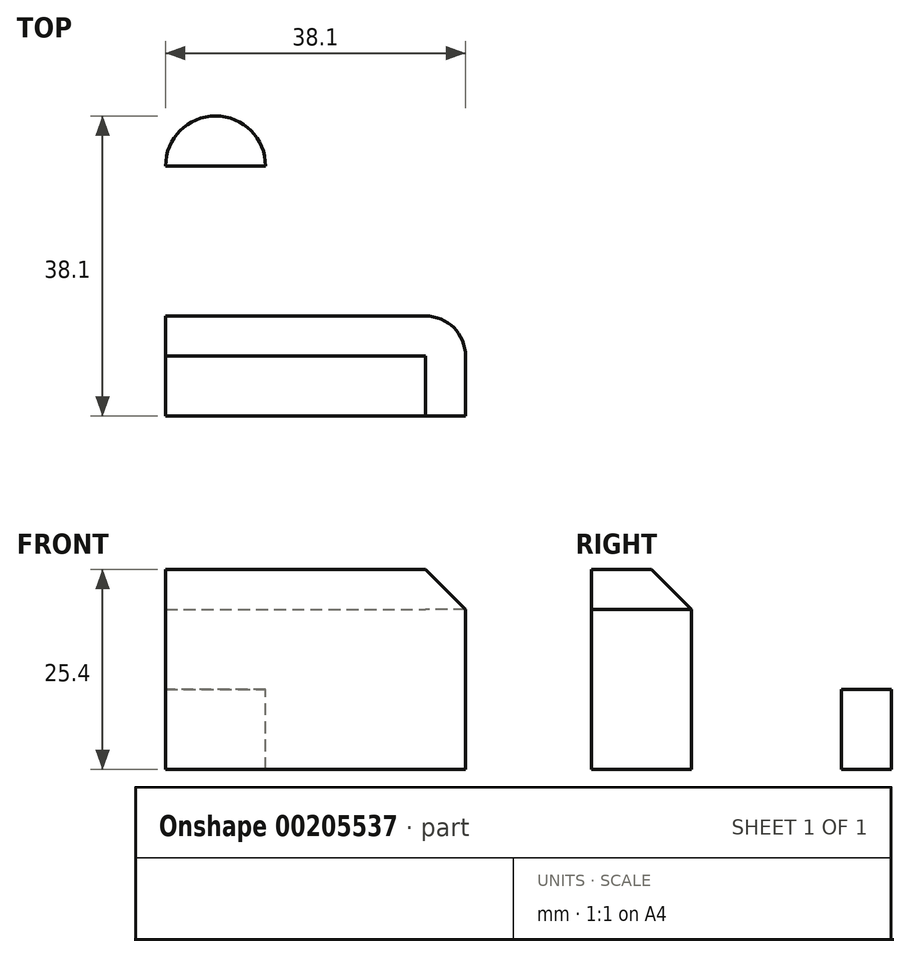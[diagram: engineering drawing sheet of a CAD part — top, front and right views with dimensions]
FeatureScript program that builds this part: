
annotation { "Feature Type Name" : "Feature", "Feature Type Description" : "" }
export const myFeature = defineFeature(function(context is Context, id is Id, definition is map)
    precondition{}
    {
        {
            var Q0;
            Q0=qCreatedBy(makeId("Top.planeOp"),FACE);
            var sketch = newSketch(context, id + "F0", { "sketchPlane" : qUnion([Q0])});
            skPoint(sketch, "E0.middle", {"position": v(0, 0) * mm});
            skLineSegment(sketch, "E1.bottom", {"start": v(-19.05, -6.35) * mm, "end": v(19.05, -6.35) * mm});
            skLineSegment(sketch, "E1.top", {"start": v(-19.05, 6.35) * mm, "end": v(19.05, 6.35) * mm});
            skLineSegment(sketch, "E1.left", {"start": v(-19.05, -6.35) * mm, "end": v(-19.05, 6.35) * mm});
            skLineSegment(sketch, "E1.right", {"start": v(19.05, -6.35) * mm, "end": v(19.05, 6.35) * mm});
            skLineSegment(sketch, "E2.bottom", {"start": v(-19.05, 6.35) * mm, "end": v(-6.35, 6.35) * mm});
            skLineSegment(sketch, "E2.top", {"start": v(-19.05, 25.4) * mm, "end": v(-6.35, 25.4) * mm});
            skLineSegment(sketch, "E2.left", {"start": v(-19.05, 6.35) * mm, "end": v(-19.05, 25.4) * mm});
            skLineSegment(sketch, "E2.right", {"start": v(-6.35, 6.35) * mm, "end": v(-6.35, 25.4) * mm});
            skArc(sketch, "E3", {"start": v(-19.05, 25.4) * mm, "mid": v(-12.7, 31.75) * mm, "end": v(-6.35, 25.4) * mm});
            skSolve(sketch);
        }
        {
            var Q0;
            Q0=makeQuery(id+"F0.imprint","IMPRINT",FACE,{"disambiguationData":[TD([[makeQuery(id+"F0.imprint","IMPRINT",EDGE,{"derivedFrom":sQuery(id+"F0.wireOp",EDGE,"E1.bottom")}),1.0]])]});
            var Q1;
            Q1=makeQuery(id+"F0.imprint","IMPRINT",FACE,{"disambiguationData":[TD([[makeQuery(id+"F0.imprint","IMPRINT",EDGE,{"derivedFrom":sQuery(id+"F0.wireOp",EDGE,"E2.bottom")}),1.0]])]});
            var Q2;
            Q2=makeQuery(id+"F0.imprint","IMPRINT",FACE,{"disambiguationData":[TD([[makeQuery(id+"F0.imprint","IMPRINT",EDGE,{"derivedFrom":sQuery(id+"F0.wireOp",EDGE,"E2.top")}),1.0]])]});
            extrude(context, id + "F1", {"entities" : qUnion([Q0, Q1, Q2]), "oppositeDirection" : true, "depth" : 25.4 * mm});
        }
        {
            var Q0;
            Q0=makeQuery(id+"F0.imprint","IMPRINT",FACE,{"disambiguationData":[TD([[makeQuery(id+"F0.imprint","IMPRINT",EDGE,{"derivedFrom":sQuery(id+"F0.wireOp",EDGE,"E2.bottom")}),1.0]])]});
            var Q1;
            Q1=makeQuery(id+"F0.imprint","IMPRINT",FACE,{"disambiguationData":[TD([[makeQuery(id+"F0.imprint","IMPRINT",EDGE,{"derivedFrom":sQuery(id+"F0.wireOp",EDGE,"E2.top")}),1.0]])]});
            extrude(context, id + "F2", {"entities" : qUnion([Q0, Q1]), "operationType" : NewBodyOperationType.REMOVE, "oppositeDirection" : true, "depth" : 15.24 * mm});
        }
        {
            var Q0;
            Q0=sQuery(id+"F0.wireOp",VERTEX,"E3.center");
            var Q1;
            Q1=makeQuery(id+"F1.opExtrude","SWEPT_BODY",BODY,{"disambiguationData":[OSD([sQuery(id+"F0.wireOp",EDGE,"E1.bottom"),sQuery(id+"F0.wireOp",EDGE,"E1.top"),sQuery(id+"F0.wireOp",EDGE,"E1.left"),sQuery(id+"F0.wireOp",EDGE,"E1.right"),sQuery(id+"F0.wireOp",EDGE,"E2.left"),sQuery(id+"F0.wireOp",EDGE,"E2.right"),sQuery(id+"F0.wireOp",EDGE,"E3")])]});
            hole(context, id + "F3", {"style" : HoleStyle.C_SINK, "endStyle" : HoleEndStyle.THROUGH, "standardTappedOrClearance" : lookupTablePath({ "standard" : "ANSI", "engagement" : "75%", "pitch" : "32 tpi", "size" : "#8", "type" : "Tapped" }), "standardBlindInLast" : lookupTablePath({ "standard" : "ANSI", "engagement" : "75%", "pitch" : "32 tpi", "size" : "#8", "type" : "Tapped" }), "holeDiameter" : 3.45 * mm, "cSinkDiameter" : 9.12 * mm, "cSinkAngle" : 82 * degree, "locations" : qUnion([Q0]), "scope" : qUnion([Q1]), "isTappedThrough" : true, "majorDiameter" : 4.17 * mm, "showTappedDepth" : true});
        }
        {
            var Q0;
            Q0=makeQuery(id+"F1.opExtrude","SWEPT_EDGE",EDGE,{"disambiguationData":[OSD([sQuery(id+"F0.wireOp",EDGE,"E1.top"),sQuery(id+"F0.wireOp",EDGE,"E2.bottom"),sQuery(id+"F0.wireOp",EDGE,"E2.right")])]});
            fillet(context, id + "F4", {"entities" : qUnion([Q0]), "radius" : 5.08 * mm, "tangentPropagation" : true, "allowEdgeOverflow" : false});
        }
        {
            var Q0;
            Q0=makeQuery(id+"F1.opExtrude","CAP_EDGE",EDGE,{"disambiguationData":[OSD([sQuery(id+"F0.wireOp",EDGE,"E1.right")])],"isStart":true});
            chamfer(context, id + "F5", {"entities" : qUnion([Q0]), "width" : 5.08 * mm, "tangentPropagation" : true});
        }
    });
